# Revit family: BOS-Leibungszarge-Planar-TEud-STW_Familie
name_source: partatom
category: Türen
revit_build: Autodesk Revit 2017 (Build: 20160225_1515(x64)
units: mm (PartAtom-declared; Revit-internal decimal feet)

## family parameters
Basisbauteil = Wand
Beim Laden mit Abzugskörper schneiden = Nein
Gemeinsam genutzt = Nein
Immer vertikal = Ja
Raumberechnungspunkt = Ja

## types (3) — shared parameters
Allgemeine Informationen zu Stahlzargen = www.BestOfSteel.de/tools-downloads/info-flyer/
BBL1 Bandbezugslinie   Hinge Position 1 = 241 mm  [stored 0.790682 ft]
BE max. = 100 mm  [stored 0.328084 ft]
Bauelement = BOS Stahlzarge
FMB max. = 1341 mm  [stored 4.39961 ft]
FMB min. = 591 mm  [stored 1.93898 ft]
FMH max. = 2858 mm  [stored 9.37664 ft]
FMH min. = 1608 mm  [stored 5.27559 ft]
Falzaufschlag = 15 mm  [stored 0.0492126 ft]
Funktion = Innen
Hersteller = BOS GmbH Best Of Steel, Lütkenfelde 4, D-48282 Emsdetten
Info-Texte sichtbar = Ja
Information in English = Nein
Material = grundiert, feuerverzinktes Feinblech nach DIN EN 10143
Material - Bänder = <Nach Kategorie>
Material - Dichtung = <Nach Kategorie>
Material - Drückergarnitur = <Nach Kategorie>
Material - Türblatt = <Nach Kategorie>
Material - Zarge = <Nach Kategorie>
Profilverschiebung = 27 mm  [stored 0.0885827 ft]
Putzwinkel hinten = 10 mm  [stored 0.0328084 ft]
Putzwinkel vorne = 10 mm  [stored 0.0328084 ft]
Tectusbänderabstand = 40 mm  [stored 0.131234 ft]
Türblattstärke 3 = 25 mm  [stored 0.082021 ft]
Türblattversatz = 67.5 mm  [stored 0.221457 ft]
URL = www.BestOfSteel.de/stahlzargen/sonderzargen-fuer-drehfluegeltueren/leibungszargen-planar/
Wandstärke min. = 125 mm  [stored 0.410105 ft]
zero-valued in all types: Breite, Dicke, Rohbaubreite, Rohbauhöhe

## per-type parameters (varying)
| type | Beschreibung | Falztiefe | Modell | TEsd (Bandrolle sichtbar) | TEsd (versteckt liegendes Band) | TEud | Tectus Bänder | Türblattstärke 1 | Türblattstärke 2 | VX Bänder gefälzt | VX Bänder stumpf |
| Gefälzt einschlagendes Türblatt | Leibungszarge Planar als Eckzarge für Ständerwerk Variante 1, gefälzt | 28.5 mm  [stored 0.0935039 ft] | TEud | Nein | Nein | Ja | Nein | 14.5 mm  [stored 0.0475722 ft] | 25.5 mm | Ja | Nein |
| Stumpf einschlagendes Türblatt (Bandrolle sichtbar) | Leibungszarge Planar als Eckzarge für Ständerwerk Variante 1, stumpf (Bandrolle sichtbar) | 46.5 mm  [stored 0.152559 ft] | TEsd | Ja | Nein | Nein | Nein | 0 mm  [stored 0 ft] | 40 mm  [stored 0.131234 ft] | Nein | Ja |
| Stumpf einschlagendes Türblatt (verdeckt liegendes Band) | Leibungszarge Planar als Eckzarge für Ständerwerk Variante 1, stumpf (verdeckt liegendes Band) | 46.5 mm  [stored 0.152559 ft] | TEsd | Nein | Ja | Nein | Ja | 0 mm  [stored 0 ft] | 40 mm  [stored 0.131234 ft] | Nein | Nein |

note: [stored X ft] marks values corroborated as IEEE doubles in the binary element streams (Revit-internal decimal feet)
